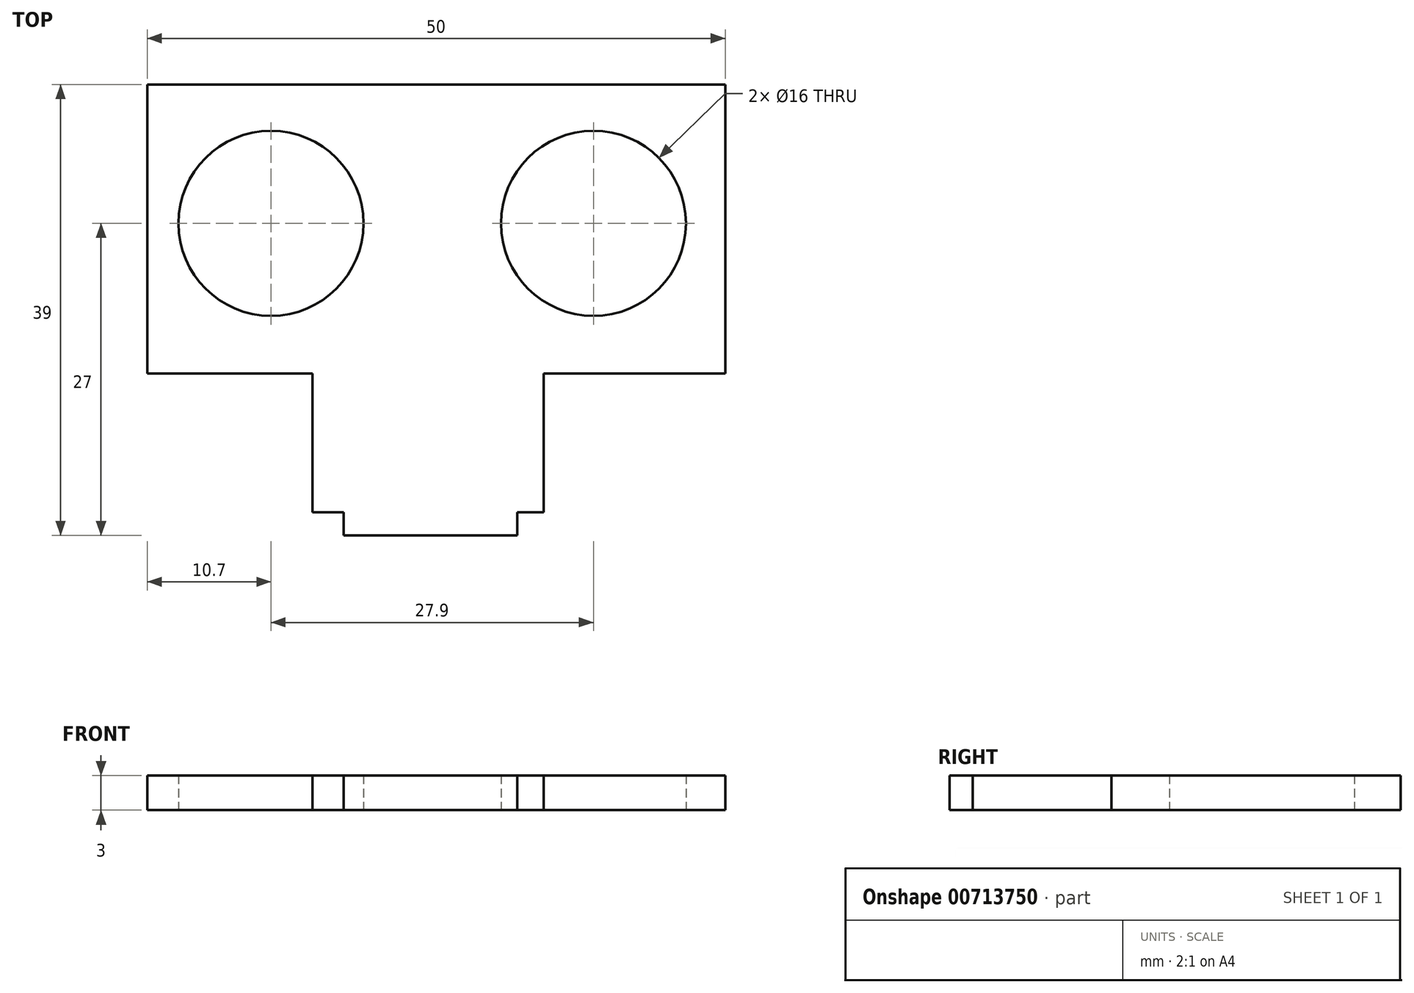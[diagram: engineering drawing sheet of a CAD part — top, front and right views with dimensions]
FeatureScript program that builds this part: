
annotation { "Feature Type Name" : "Feature", "Feature Type Description" : "" }
export const myFeature = defineFeature(function(context is Context, id is Id, definition is map)
    precondition{}
    {
        {
            var Q0;
            Q0=qCreatedBy(makeId("Top.planeOp"),FACE);
            var sketch = newSketch(context, id + "F0", { "sketchPlane" : qUnion([Q0])});
            skLineSegment(sketch, "E0.bottom", {"start": v(-24.05, 51) * mm, "end": v(25.95, 51) * mm});
            skLineSegment(sketch, "E0.top", {"start": v(-24.05, 26) * mm, "end": v(25.95, 26) * mm});
            skLineSegment(sketch, "E0.left", {"start": v(-24.05, 51) * mm, "end": v(-24.05, 26) * mm});
            skLineSegment(sketch, "E0.right", {"start": v(25.95, 51) * mm, "end": v(25.95, 26) * mm});
            skCircle(sketch, "E1", {"center": v(-13.35, 39) * mm, "radius": 8 * mm});
            skCircle(sketch, "E2", {"center": v(14.55, 39) * mm, "radius": 8 * mm});
            skLineSegment(sketch, "E3.bottom", {"start": v(-9.75, 26) * mm, "end": v(10.25, 26) * mm});
            skLineSegment(sketch, "E3.top", {"start": v(-9.75, 14) * mm, "end": v(10.25, 14) * mm});
            skLineSegment(sketch, "E3.left", {"start": v(-9.75, 26) * mm, "end": v(-9.75, 14) * mm});
            skLineSegment(sketch, "E3.right", {"start": v(10.25, 26) * mm, "end": v(10.25, 14) * mm});
            skLineSegment(sketch, "E4.bottom", {"start": v(-7.05, 14) * mm, "end": v(7.95, 14) * mm});
            skLineSegment(sketch, "E4.top", {"start": v(-7.05, 12) * mm, "end": v(7.95, 12) * mm});
            skLineSegment(sketch, "E4.left", {"start": v(-7.05, 14) * mm, "end": v(-7.05, 12) * mm});
            skLineSegment(sketch, "E4.right", {"start": v(7.95, 14) * mm, "end": v(7.95, 12) * mm});
            skSolve(sketch);
        }
        {
            var Q0;
            Q0 = qSketchRegion(id + "F0", true);
            extrude(context, id + "F1", {"entities" : qUnion([Q0]), "depth" : 3 * mm, "offsetDistance" : 25 * mm});
        }
    });
